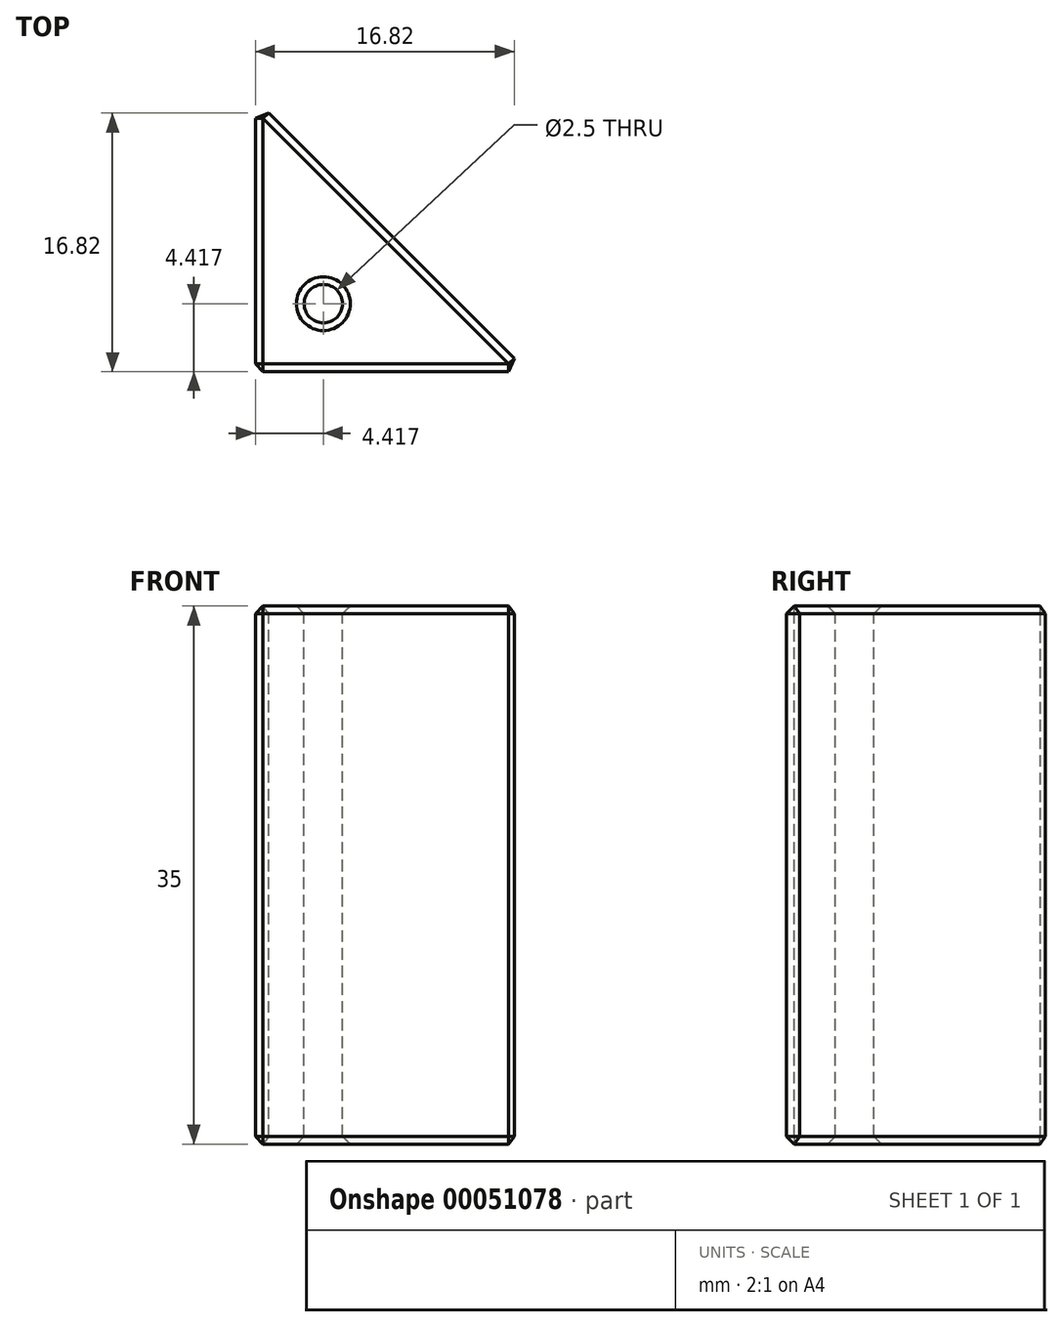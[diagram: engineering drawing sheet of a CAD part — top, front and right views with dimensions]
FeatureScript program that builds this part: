
annotation { "Feature Type Name" : "Feature", "Feature Type Description" : "" }
export const myFeature = defineFeature(function(context is Context, id is Id, definition is map)
    precondition{}
    {
        {
            var Q0;
            Q0=qCreatedBy(makeId("Top.planeOp"),FACE);
            var sketch = newSketch(context, id + "F0", { "sketchPlane" : qUnion([Q0])});
            skLineSegment(sketch, "E0.bottom", {"start": v(0, 0) * mm, "end": v(17.68, 0) * mm});
            skLineSegment(sketch, "E0.top", {"start": v(0, 17.68) * mm, "end": v(17.68, 17.68) * mm});
            skLineSegment(sketch, "E0.left", {"start": v(0, 0) * mm, "end": v(0, 17.68) * mm});
            skLineSegment(sketch, "E0.right", {"start": v(17.68, 0) * mm, "end": v(17.68, 17.68) * mm});
            skSolve(sketch);
        }
        {
            var Q0;
            Q0 = qSketchRegion(id + "F0", true);
            extrude(context, id + "F1", {"entities" : qUnion([Q0]), "depth" : 35 * mm});
        }
        {
            var Q0;
            Q0=makeQuery(id+"F1.opExtrude","CAP_FACE",FACE,{"disambiguationData":[OSD([sQuery(id+"F0.wireOp",EDGE,"E0.bottom"),sQuery(id+"F0.wireOp",EDGE,"E0.top"),sQuery(id+"F0.wireOp",EDGE,"E0.left"),sQuery(id+"F0.wireOp",EDGE,"E0.right")])],"isStart":false});
            var sketch = newSketch(context, id + "F2", { "sketchPlane" : qUnion([Q0])});
            skLineSegment(sketch, "E1", {"start": v(0, 17.68) * mm, "end": v(0, 0) * mm});
            skLineSegment(sketch, "E2", {"start": v(0, 0) * mm, "end": v(17.68, 0) * mm});
            skLineSegment(sketch, "E3", {"start": v(17.68, 0) * mm, "end": v(0, 17.68) * mm});
            skSolve(sketch);
        }
        {
            var Q0;
            Q0=makeQuery(id+"F2.imprint","IMPRINT",FACE,{"disambiguationData":[TD([[makeQuery(id+"F2.imprint","IMPRINT",EDGE,{"derivedFrom":sQuery(id+"F2.wireOp",EDGE,"E3")}),-1.0]])]});
            extrude(context, id + "F3", {"entities" : qUnion([Q0]), "operationType" : NewBodyOperationType.REMOVE, "oppositeDirection" : true, "depth" : 35 * mm});
        }
        {
            var Q0;
            Q0=makeQuery(id+"F1.opExtrude","CAP_FACE",FACE,{"disambiguationData":[OSD([sQuery(id+"F0.wireOp",EDGE,"E0.bottom"),sQuery(id+"F0.wireOp",EDGE,"E0.top"),sQuery(id+"F0.wireOp",EDGE,"E0.left"),sQuery(id+"F0.wireOp",EDGE,"E0.right")])],"isStart":false});
            var sketch = newSketch(context, id + "F4", { "sketchPlane" : qUnion([Q0])});
            skCircle(sketch, "E4", {"center": v(4.42, 4.42) * mm, "radius": 1.25 * mm});
            skSolve(sketch);
        }
        {
            var Q0;
            Q0 = qSketchRegion(id + "F4", true);
            extrude(context, id + "F5", {"entities" : qUnion([Q0]), "operationType" : NewBodyOperationType.REMOVE, "oppositeDirection" : true, "depth" : 35 * mm});
        }
        {
            var Q0;
            Q0=makeQuery(id+"F3.boolean.opBoolean","COPY",FACE,{"derivedFrom":makeQuery(id+"F3.opExtrude","SWEPT_FACE",FACE,{"disambiguationData":[OSD([sQuery(id+"F2.wireOp",EDGE,"E3")])]})});
            var Q1;
            Q1=makeQuery(id+"F1.opExtrude","CAP_FACE",FACE,{"disambiguationData":[OSD([sQuery(id+"F0.wireOp",EDGE,"E0.bottom"),sQuery(id+"F0.wireOp",EDGE,"E0.top"),sQuery(id+"F0.wireOp",EDGE,"E0.left"),sQuery(id+"F0.wireOp",EDGE,"E0.right")])],"isStart":false});
            var Q2;
            Q2=makeQuery(id+"F1.opExtrude","CAP_FACE",FACE,{"disambiguationData":[OSD([sQuery(id+"F0.wireOp",EDGE,"E0.bottom"),sQuery(id+"F0.wireOp",EDGE,"E0.top"),sQuery(id+"F0.wireOp",EDGE,"E0.left"),sQuery(id+"F0.wireOp",EDGE,"E0.right")])],"isStart":true});
            var Q3;
            Q3=makeQuery(id+"F1.opExtrude","SWEPT_FACE",FACE,{"disambiguationData":[OSD([sQuery(id+"F0.wireOp",EDGE,"E0.bottom")])]});
            var Q4;
            Q4=makeQuery(id+"F1.opExtrude","SWEPT_FACE",FACE,{"disambiguationData":[OSD([sQuery(id+"F0.wireOp",EDGE,"E0.left")])]});
            chamfer(context, id + "F6", {"entities" : qUnion([Q0, Q1, Q2, Q3, Q4]), "width" : 0.5 * mm, "tangentPropagation" : true});
        }
    });
